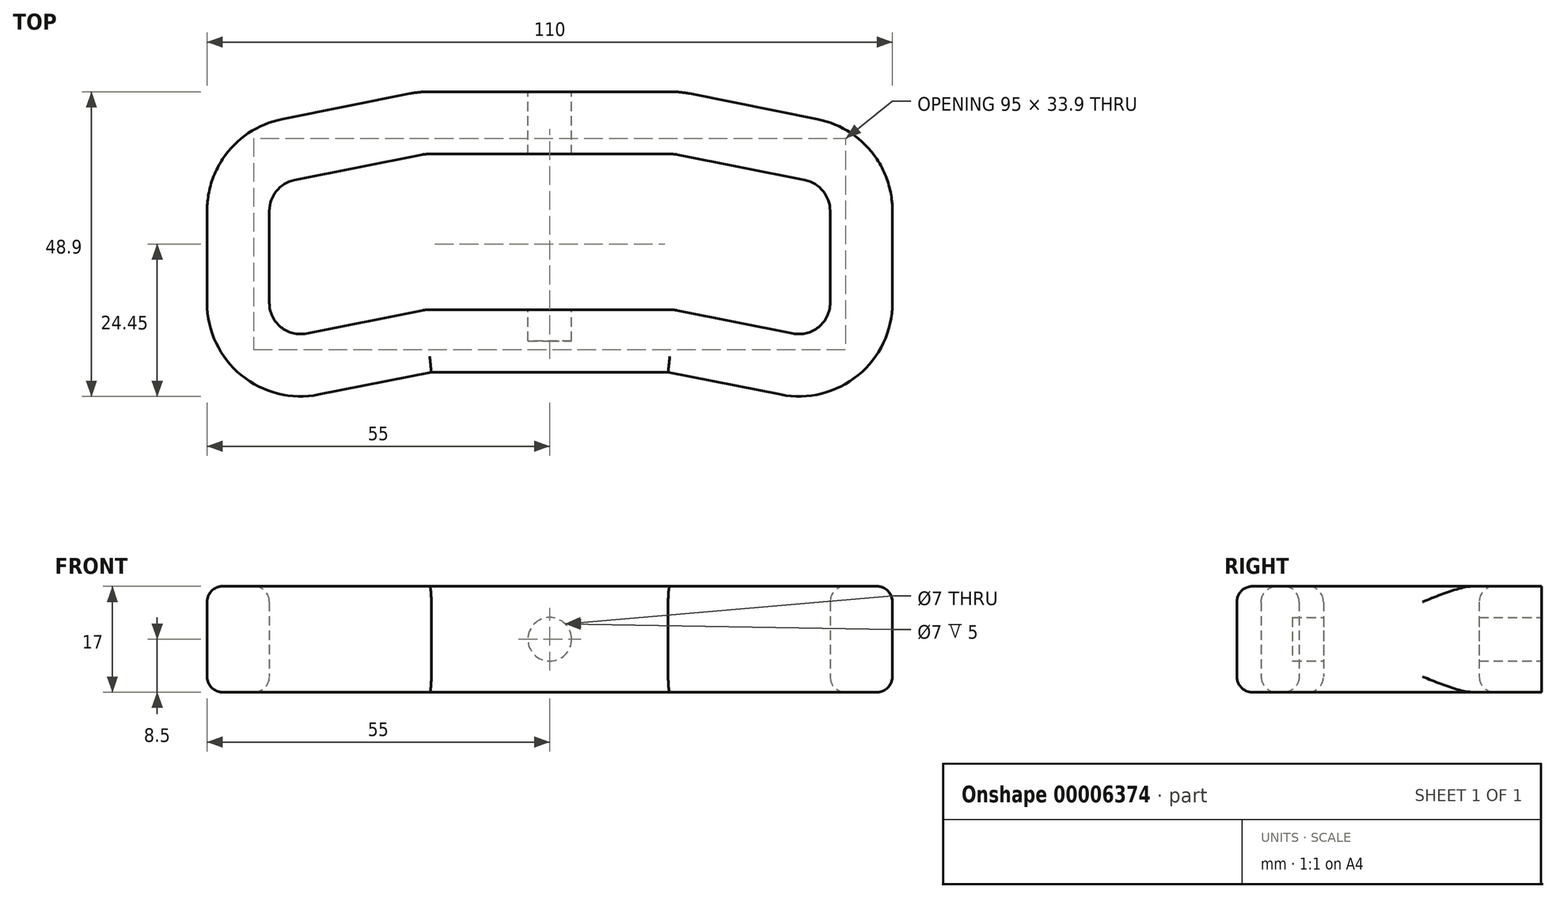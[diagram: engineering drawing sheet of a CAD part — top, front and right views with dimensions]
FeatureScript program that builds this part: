
annotation { "Feature Type Name" : "Feature", "Feature Type Description" : "" }
export const myFeature = defineFeature(function(context is Context, id is Id, definition is map)
    precondition{}
    {
        {
            var Q0;
            Q0=qCreatedBy(makeId("Top.planeOp"),FACE);
            var sketch = newSketch(context, id + "F0", { "sketchPlane" : qUnion([Q0])});
            skLineSegment(sketch, "E0.bottom", {"start": v(-45, 30) * mm, "end": v(45, 30) * mm, "construction": true});
            skLineSegment(sketch, "E0.top", {"start": v(-45, 0) * mm, "end": v(45, 0) * mm, "construction": true});
            skLineSegment(sketch, "E0.left", {"start": v(-45, 30) * mm, "end": v(-45, 0) * mm, "construction": true});
            skLineSegment(sketch, "E0.right", {"start": v(45, 30) * mm, "end": v(45, 0) * mm, "construction": true});
            skLineSegment(sketch, "E1.bottom", {"start": v(-20, 30) * mm, "end": v(20, 30) * mm, "construction": true});
            skLineSegment(sketch, "E1.top", {"start": v(-20, 0) * mm, "end": v(20, 0) * mm, "construction": true});
            skLineSegment(sketch, "E1.left", {"start": v(-20, 30) * mm, "end": v(-20, 0) * mm, "construction": true});
            skLineSegment(sketch, "E1.right", {"start": v(20, 30) * mm, "end": v(20, 0) * mm, "construction": true});
            skLineSegment(sketch, "E2.bottom", {"start": v(-45, 25) * mm, "end": v(45, 25) * mm, "construction": true});
            skLineSegment(sketch, "E2.top", {"start": v(-45, 5) * mm, "end": v(45, 5) * mm, "construction": true});
            skLineSegment(sketch, "E2.left", {"start": v(-45, 25) * mm, "end": v(-45, 5) * mm, "construction": true});
            skLineSegment(sketch, "E2.right", {"start": v(45, 25) * mm, "end": v(45, 5) * mm, "construction": true});
            skLineSegment(sketch, "E3", {"start": v(-40.98, 25.8) * mm, "end": v(-20.49, 29.9) * mm});
            skLineSegment(sketch, "E4", {"start": v(20.49, 29.9) * mm, "end": v(40.98, 25.8) * mm});
            skLineSegment(sketch, "E5", {"start": v(-19.5, 30) * mm, "end": v(19.5, 30) * mm});
            skLineSegment(sketch, "E6", {"start": v(39.02, 1.2) * mm, "end": v(20.49, 4.9) * mm});
            skLineSegment(sketch, "E7", {"start": v(-19.5, 5) * mm, "end": v(19.5, 5) * mm});
            skLineSegment(sketch, "E8", {"start": v(-20.49, 4.9) * mm, "end": v(-39.02, 1.2) * mm});
            skLineSegment(sketch, "E9", {"start": v(-45, 6.1) * mm, "end": v(-45, 20.9) * mm});
            skPoint(sketch, "E10.visualSharp", {"position": v(-45, 25) * mm});
            skArc(sketch, "E10.filletArc", {"start": v(-40.98, 25.8) * mm, "mid": v(-43.87, 24.07) * mm, "end": v(-45, 20.9) * mm});
            skPoint(sketch, "E11.visualSharp", {"position": v(-45, 0) * mm});
            skArc(sketch, "E11.filletArc", {"start": v(-45, 6.1) * mm, "mid": v(-43.17, 2.23) * mm, "end": v(-39.02, 1.2) * mm});
            skPoint(sketch, "E12.visualSharp", {"position": v(-20, 5) * mm});
            skArc(sketch, "E12.filletArc", {"start": v(-19.5, 5) * mm, "mid": v(-20, 4.98) * mm, "end": v(-20.49, 4.9) * mm});
            skPoint(sketch, "E13.visualSharp", {"position": v(20, 5) * mm});
            skArc(sketch, "E13.filletArc", {"start": v(20.49, 4.9) * mm, "mid": v(20, 4.98) * mm, "end": v(19.5, 5) * mm});
            skLineSegment(sketch, "E14", {"start": v(45, 6.1) * mm, "end": v(45, 20.9) * mm});
            skPoint(sketch, "E15.visualSharp", {"position": v(45, 0) * mm});
            skArc(sketch, "E15.filletArc", {"start": v(39.02, 1.2) * mm, "mid": v(43.17, 2.23) * mm, "end": v(45, 6.1) * mm});
            skPoint(sketch, "E16.visualSharp", {"position": v(45, 25) * mm});
            skArc(sketch, "E16.filletArc", {"start": v(45, 20.9) * mm, "mid": v(43.87, 24.07) * mm, "end": v(40.98, 25.8) * mm});
            skPoint(sketch, "E17.visualSharp", {"position": v(20, 30) * mm});
            skArc(sketch, "E17.filletArc", {"start": v(20.49, 29.9) * mm, "mid": v(20, 29.98) * mm, "end": v(19.5, 30) * mm});
            skPoint(sketch, "E18.visualSharp", {"position": v(-20, 30) * mm});
            skArc(sketch, "E18.filletArc", {"start": v(-19.5, 30) * mm, "mid": v(-20, 29.98) * mm, "end": v(-20.49, 29.9) * mm});
            skArc(sketch, "E19.0", {"start": v(-55, 6.1) * mm, "mid": v(-49.5, -5.5) * mm, "end": v(-37.06, -8.6) * mm});
            skLineSegment(sketch, "E19.1", {"start": v(-19, -5) * mm, "end": v(-37.06, -8.6) * mm});
            skLineSegment(sketch, "E19.2", {"start": v(-19, -5) * mm, "end": v(19, -5) * mm});
            skLineSegment(sketch, "E19.3", {"start": v(37.06, -8.6) * mm, "end": v(19, -5) * mm});
            skArc(sketch, "E19.4", {"start": v(37.06, -8.6) * mm, "mid": v(49.5, -5.5) * mm, "end": v(55, 6.1) * mm});
            skLineSegment(sketch, "E19.5", {"start": v(-55, 6.1) * mm, "end": v(-55, 20.9) * mm});
            skLineSegment(sketch, "E19.6", {"start": v(55, 6.1) * mm, "end": v(55, 20.9) * mm});
            skArc(sketch, "E19.7", {"start": v(55, 20.9) * mm, "mid": v(51.6, 30.41) * mm, "end": v(42.94, 35.6) * mm});
            skLineSegment(sketch, "E19.8", {"start": v(22.45, 39.7) * mm, "end": v(42.94, 35.6) * mm});
            skArc(sketch, "E19.9", {"start": v(22.45, 39.7) * mm, "mid": v(20.98, 39.93) * mm, "end": v(19.5, 40) * mm});
            skLineSegment(sketch, "E19.10", {"start": v(-19.5, 40) * mm, "end": v(19.5, 40) * mm});
            skArc(sketch, "E19.11", {"start": v(-19.5, 40) * mm, "mid": v(-20.98, 39.93) * mm, "end": v(-22.45, 39.7) * mm});
            skLineSegment(sketch, "E19.12", {"start": v(-42.94, 35.6) * mm, "end": v(-22.45, 39.7) * mm});
            skArc(sketch, "E19.13", {"start": v(-42.94, 35.6) * mm, "mid": v(-51.6, 30.41) * mm, "end": v(-55, 20.9) * mm});
            skLineSegment(sketch, "E20", {"start": v(-221.78, -63.4) * mm, "end": v(-201.28, -59.3) * mm});
            skLineSegment(sketch, "E21", {"start": v(-200.3, -59.2) * mm, "end": v(-161.3, -59.2) * mm});
            skLineSegment(sketch, "E22", {"start": v(-200.3, -84.2) * mm, "end": v(-161.3, -84.2) * mm});
            skLineSegment(sketch, "E23", {"start": v(-201.28, -84.3) * mm, "end": v(-219.82, -88) * mm});
            skLineSegment(sketch, "E24", {"start": v(-225.8, -83.1) * mm, "end": v(-225.8, -68.3) * mm});
            skPoint(sketch, "E25.visualSharp", {"position": v(-225.8, -64.2) * mm});
            skArc(sketch, "E25.filletArc", {"start": v(-221.78, -63.4) * mm, "mid": v(-224.66, -65.13) * mm, "end": v(-225.8, -68.3) * mm});
            skPoint(sketch, "E26.visualSharp", {"position": v(-225.8, -89.2) * mm});
            skArc(sketch, "E26.filletArc", {"start": v(-225.8, -83.1) * mm, "mid": v(-223.97, -86.97) * mm, "end": v(-219.82, -88) * mm});
            skPoint(sketch, "E27.visualSharp", {"position": v(-200.8, -84.2) * mm});
            skArc(sketch, "E27.filletArc", {"start": v(-200.3, -84.2) * mm, "mid": v(-200.8, -84.22) * mm, "end": v(-201.28, -84.3) * mm});
            skPoint(sketch, "E28.visualSharp", {"position": v(-200.8, -59.2) * mm});
            skArc(sketch, "E28.filletArc", {"start": v(-200.3, -59.2) * mm, "mid": v(-200.8, -59.22) * mm, "end": v(-201.28, -59.3) * mm});
            skArc(sketch, "E29.0", {"start": v(-235.8, -83.1) * mm, "mid": v(-234.65, -88.85) * mm, "end": v(-231.38, -93.73) * mm});
            skLineSegment(sketch, "E29.5", {"start": v(-235.8, -83.1) * mm, "end": v(-235.8, -68.3) * mm});
            skLineSegment(sketch, "E29.10", {"start": v(-200.3, -49.2) * mm, "end": v(-161.3, -49.2) * mm, "construction": true});
            skArc(sketch, "E29.11", {"start": v(-200.3, -49.2) * mm, "mid": v(-201.78, -49.27) * mm, "end": v(-203.24, -49.5) * mm, "construction": true});
            skLineSegment(sketch, "E29.12", {"start": v(-223.74, -53.6) * mm, "end": v(-203.24, -49.5) * mm, "construction": true});
            skArc(sketch, "E29.13", {"start": v(-223.74, -53.6) * mm, "mid": v(-232.4, -58.79) * mm, "end": v(-235.8, -68.3) * mm, "construction": true});
            skPoint(sketch, "E30", {"position": v(-231.38, -93.73) * mm});
            skLineSegment(sketch, "E31.MirrorCS", {"start": v(-200.8, -44.2) * mm, "end": v(-160.8, -44.2) * mm});
            skLineSegment(sketch, "E32.MirrorCS", {"start": v(-235.8, -65.3) * mm, "end": v(-235.8, -80.1) * mm});
            skArc(sketch, "E33.MirrorCS", {"start": v(-235.8, -65.3) * mm, "mid": v(-233.22, -56.89) * mm, "end": v(-226.37, -51.37) * mm});
            skLineSegment(sketch, "E34", {"start": v(-231.38, -93.73) * mm, "end": v(-202.8, -122.21) * mm});
            skLineSegment(sketch, "E35", {"start": v(-200.8, -44.2) * mm, "end": v(-226.37, -51.37) * mm});
            skArc(sketch, "E36", {"start": v(-200.8, -44.2) * mm, "mid": v(-194.13, -49.2) * mm, "end": v(-187.46, -44.2) * mm, "construction": true});
            skArc(sketch, "E37", {"start": v(-187.46, -44.2) * mm, "mid": v(-180.8, -49.2) * mm, "end": v(-174.13, -44.2) * mm, "construction": true});
            skArc(sketch, "E38", {"start": v(-213.64, -47.8) * mm, "mid": v(-206.08, -50.04) * mm, "end": v(-200.8, -44.2) * mm, "construction": true});
            skArc(sketch, "E39", {"start": v(-226.47, -51.4) * mm, "mid": v(-219.2, -52.66) * mm, "end": v(-213.64, -47.8) * mm, "construction": true});
            skArc(sketch, "E40", {"start": v(-235.28, -61.4) * mm, "mid": v(-230.53, -56.71) * mm, "end": v(-226.47, -51.4) * mm, "construction": true});
            skPoint(sketch, "E41.visualSharp", {"position": v(-200.8, -124.2) * mm});
            skArc(sketch, "E41.filletArc", {"start": v(-202.8, -122.21) * mm, "mid": v(-200.23, -123.83) * mm, "end": v(-197.21, -124.2) * mm});
            skLineSegment(sketch, "E42.4", {"start": v(-200.3, -62.4) * mm, "end": v(-161.3, -62.4) * mm, "construction": true});
            skArc(sketch, "E42.5", {"start": v(-200.3, -62.4) * mm, "mid": v(-200.48, -62.4) * mm, "end": v(-200.66, -62.43) * mm});
            skLineSegment(sketch, "E42.6", {"start": v(-221.15, -66.53) * mm, "end": v(-200.66, -62.43) * mm, "construction": true});
            skArc(sketch, "E42.7", {"start": v(-221.15, -66.53) * mm, "mid": v(-222.2, -67.16) * mm, "end": v(-222.6, -68.3) * mm, "construction": true});
            skLineSegment(sketch, "E42.8", {"start": v(-222.6, -83.1) * mm, "end": v(-222.6, -68.3) * mm, "construction": true});
            skArc(sketch, "E42.9", {"start": v(-222.6, -83.1) * mm, "mid": v(-221.94, -84.5) * mm, "end": v(-220.45, -84.87) * mm, "construction": true});
            skLineSegment(sketch, "E42.10", {"start": v(-201.91, -81.16) * mm, "end": v(-220.45, -84.87) * mm, "construction": true});
            skArc(sketch, "E42.11", {"start": v(-200.3, -81) * mm, "mid": v(-201.11, -81.04) * mm, "end": v(-201.91, -81.16) * mm, "construction": true});
            skLineSegment(sketch, "E42.12", {"start": v(-200.3, -81) * mm, "end": v(-161.3, -81) * mm, "construction": true});
            skLineSegment(sketch, "E43", {"start": v(-180.8, -42.26) * mm, "end": v(-180.8, -30.31) * mm, "construction": true});
            skArc(sketch, "E44.MirrorCS", {"start": v(-161.3, -84.2) * mm, "mid": v(-160.8, -84.22) * mm, "end": v(-160.31, -84.3) * mm});
            skArc(sketch, "E45.MirrorCS", {"start": v(-161.3, -59.2) * mm, "mid": v(-160.8, -59.22) * mm, "end": v(-160.31, -59.3) * mm});
            skArc(sketch, "E46.MirrorCS", {"start": v(-140.45, -66.53) * mm, "mid": v(-139.4, -67.16) * mm, "end": v(-139, -68.3) * mm, "construction": true});
            skArc(sketch, "E47.MirrorCS", {"start": v(-161.3, -49.2) * mm, "mid": v(-159.82, -49.27) * mm, "end": v(-158.35, -49.5) * mm, "construction": true});
            skArc(sketch, "E48.MirrorCS", {"start": v(-161.3, -62.4) * mm, "mid": v(-161.12, -62.4) * mm, "end": v(-160.94, -62.43) * mm});
            skArc(sketch, "E49.MirrorCS", {"start": v(-139, -83.1) * mm, "mid": v(-139.66, -84.5) * mm, "end": v(-141.15, -84.87) * mm, "construction": true});
            skArc(sketch, "E50.MirrorCS", {"start": v(-161.3, -81) * mm, "mid": v(-160.49, -81.04) * mm, "end": v(-159.68, -81.16) * mm, "construction": true});
            skLineSegment(sketch, "E51.MirrorCS", {"start": v(-125.8, -65.3) * mm, "end": v(-125.8, -80.1) * mm});
            skPoint(sketch, "E52.MirrorP", {"position": v(-135.8, -64.2) * mm});
            skArc(sketch, "E53.MirrorCS", {"start": v(-147.96, -47.8) * mm, "mid": v(-155.51, -50.04) * mm, "end": v(-160.8, -44.2) * mm, "construction": true});
            skLineSegment(sketch, "E54.MirrorCS", {"start": v(-159.68, -81.16) * mm, "end": v(-141.15, -84.87) * mm, "construction": true});
            skLineSegment(sketch, "E55.MirrorCS", {"start": v(-160.31, -84.3) * mm, "end": v(-141.78, -88) * mm});
            skLineSegment(sketch, "E56.MirrorCS", {"start": v(-130.21, -93.73) * mm, "end": v(-158.8, -122.21) * mm});
            skLineSegment(sketch, "E57.MirrorCS", {"start": v(-140.45, -66.53) * mm, "end": v(-160.94, -62.43) * mm, "construction": true});
            skPoint(sketch, "E58.MirrorP", {"position": v(-135.8, -89.2) * mm});
            skPoint(sketch, "E59.MirrorP", {"position": v(-160.8, -124.2) * mm});
            skLineSegment(sketch, "E60.MirrorCS", {"start": v(-125.8, -83.1) * mm, "end": v(-125.8, -68.3) * mm});
            skArc(sketch, "E61.MirrorCS", {"start": v(-135.12, -51.4) * mm, "mid": v(-142.4, -52.66) * mm, "end": v(-147.96, -47.8) * mm, "construction": true});
            skArc(sketch, "E62.MirrorCS", {"start": v(-160.8, -44.2) * mm, "mid": v(-167.46, -49.2) * mm, "end": v(-174.13, -44.2) * mm, "construction": true});
            skArc(sketch, "E63.MirrorCS", {"start": v(-126.31, -61.4) * mm, "mid": v(-131.07, -56.71) * mm, "end": v(-135.12, -51.4) * mm, "construction": true});
            skArc(sketch, "E64.MirrorCS", {"start": v(-158.8, -122.21) * mm, "mid": v(-161.37, -123.83) * mm, "end": v(-164.38, -124.2) * mm});
            skLineSegment(sketch, "E65.MirrorCS", {"start": v(-160.8, -44.2) * mm, "end": v(-135.23, -51.37) * mm});
            skPoint(sketch, "E66.MirrorP", {"position": v(-130.21, -93.73) * mm});
            skArc(sketch, "E67.MirrorCS", {"start": v(-125.8, -65.3) * mm, "mid": v(-128.38, -56.89) * mm, "end": v(-135.23, -51.37) * mm});
            skLineSegment(sketch, "E68.MirrorCS", {"start": v(-135.8, -83.1) * mm, "end": v(-135.8, -68.3) * mm});
            skArc(sketch, "E69.MirrorCS", {"start": v(-125.8, -83.1) * mm, "mid": v(-126.95, -88.85) * mm, "end": v(-130.21, -93.73) * mm});
            skPoint(sketch, "E70.MirrorP", {"position": v(-160.8, -84.2) * mm});
            skLineSegment(sketch, "E71.MirrorCS", {"start": v(-139.82, -63.4) * mm, "end": v(-160.31, -59.3) * mm});
            skLineSegment(sketch, "E72.MirrorCS", {"start": v(-137.86, -53.6) * mm, "end": v(-158.35, -49.5) * mm, "construction": true});
            skArc(sketch, "E73.MirrorCS", {"start": v(-135.8, -83.1) * mm, "mid": v(-137.63, -86.97) * mm, "end": v(-141.78, -88) * mm});
            skPoint(sketch, "E74.MirrorP", {"position": v(-160.8, -59.2) * mm});
            skArc(sketch, "E75.MirrorCS", {"start": v(-139.82, -63.4) * mm, "mid": v(-136.93, -65.13) * mm, "end": v(-135.8, -68.3) * mm});
            skLineSegment(sketch, "E76.MirrorCS", {"start": v(-139, -83.1) * mm, "end": v(-139, -68.3) * mm, "construction": true});
            skArc(sketch, "E77.MirrorCS", {"start": v(-137.86, -53.6) * mm, "mid": v(-129.2, -58.79) * mm, "end": v(-125.8, -68.3) * mm, "construction": true});
            skLineSegment(sketch, "E78", {"start": v(-197.21, -124.2) * mm, "end": v(-164.38, -124.2) * mm});
            skSolve(sketch);
        }
        {
            var Q0;
            Q0=makeQuery(id+"F0.imprint","IMPRINT",FACE,{"disambiguationData":[TD([[makeQuery(id+"F0.imprint","IMPRINT",EDGE,{"derivedFrom":sQuery(id+"F0.wireOp",EDGE,"E3")}),1.0]])]});
            extrude(context, id + "F1", {"entities" : qUnion([Q0]), "depth" : 17 * mm});
        }
        {
            var Q0;
            Q0=makeQuery(id+"F1.opExtrude","SWEPT_FACE",FACE,{"disambiguationData":[OSD([sQuery(id+"F0.wireOp",EDGE,"E19.10")])]});
            var sketch = newSketch(context, id + "F2", { "sketchPlane" : qUnion([Q0])});
            skLineSegment(sketch, "E79", {"start": v(-19.5, 17) * mm, "end": v(19.5, 0) * mm, "construction": true});
            skLineSegment(sketch, "E80", {"start": v(19.5, 17) * mm, "end": v(-19.5, 0) * mm, "construction": true});
            skCircle(sketch, "E81", {"center": v(0, 8.5) * mm, "radius": 3.5 * mm});
            skSolve(sketch);
        }
        {
            var Q0;
            Q0=makeQuery(id+"F2.imprint","IMPRINT",FACE,{"disambiguationData":[TD([[makeQuery(id+"F2.imprint","IMPRINT",EDGE,{"derivedFrom":sQuery(id+"F2.wireOp",EDGE,"E81")}),1.0]])]});
            extrude(context, id + "F3", {"entities" : qUnion([Q0]), "operationType" : NewBodyOperationType.REMOVE, "oppositeDirection" : true, "depth" : 40 * mm});
        }
        {
            var Q0;
            Q0=makeQuery(id+"F1.opExtrude","CAP_EDGE",EDGE,{"disambiguationData":[OSD([sQuery(id+"F0.wireOp",EDGE,"E5")])],"isStart":true});
            var Q1;
            Q1=makeQuery(id+"F1.opExtrude","CAP_EDGE",EDGE,{"disambiguationData":[OSD([sQuery(id+"F0.wireOp",EDGE,"E5")])],"isStart":false});
            fillet(context, id + "F4", {"entities" : qUnion([Q0, Q1]), "radius" : 2.5 * mm, "tangentPropagation" : true, "allowEdgeOverflow" : false});
        }
        {
            var Q0;
            Q0=makeQuery(id+"F1.opExtrude","CAP_EDGE",EDGE,{"disambiguationData":[OSD([sQuery(id+"F0.wireOp",EDGE,"E19.5")])],"isStart":false});
            var Q1;
            Q1=makeQuery(id+"F1.opExtrude","CAP_EDGE",EDGE,{"disambiguationData":[OSD([sQuery(id+"F0.wireOp",EDGE,"E19.0")])],"isStart":false});
            var Q2;
            Q2=makeQuery(id+"F1.opExtrude","CAP_EDGE",EDGE,{"disambiguationData":[OSD([sQuery(id+"F0.wireOp",EDGE,"E19.1")])],"isStart":false});
            var Q3;
            Q3=makeQuery(id+"F1.opExtrude","CAP_EDGE",EDGE,{"disambiguationData":[OSD([sQuery(id+"F0.wireOp",EDGE,"E19.2")])],"isStart":false});
            var Q4;
            Q4=makeQuery(id+"F1.opExtrude","CAP_EDGE",EDGE,{"disambiguationData":[OSD([sQuery(id+"F0.wireOp",EDGE,"E19.3")])],"isStart":false});
            var Q5;
            Q5=makeQuery(id+"F1.opExtrude","CAP_EDGE",EDGE,{"disambiguationData":[OSD([sQuery(id+"F0.wireOp",EDGE,"E19.4")])],"isStart":false});
            var Q6;
            Q6=makeQuery(id+"F1.opExtrude","CAP_EDGE",EDGE,{"disambiguationData":[OSD([sQuery(id+"F0.wireOp",EDGE,"E19.6")])],"isStart":false});
            var Q7;
            Q7=makeQuery(id+"F1.opExtrude","CAP_EDGE",EDGE,{"disambiguationData":[OSD([sQuery(id+"F0.wireOp",EDGE,"E19.6")])],"isStart":true});
            var Q8;
            Q8=makeQuery(id+"F1.opExtrude","CAP_EDGE",EDGE,{"disambiguationData":[OSD([sQuery(id+"F0.wireOp",EDGE,"E19.4")])],"isStart":true});
            var Q9;
            Q9=makeQuery(id+"F1.opExtrude","CAP_EDGE",EDGE,{"disambiguationData":[OSD([sQuery(id+"F0.wireOp",EDGE,"E19.3")])],"isStart":true});
            var Q10;
            Q10=makeQuery(id+"F1.opExtrude","CAP_EDGE",EDGE,{"disambiguationData":[OSD([sQuery(id+"F0.wireOp",EDGE,"E19.2")])],"isStart":true});
            var Q11;
            Q11=makeQuery(id+"F1.opExtrude","CAP_EDGE",EDGE,{"disambiguationData":[OSD([sQuery(id+"F0.wireOp",EDGE,"E19.1")])],"isStart":true});
            var Q12;
            Q12=makeQuery(id+"F1.opExtrude","CAP_EDGE",EDGE,{"disambiguationData":[OSD([sQuery(id+"F0.wireOp",EDGE,"E19.0")])],"isStart":true});
            var Q13;
            Q13=makeQuery(id+"F1.opExtrude","CAP_EDGE",EDGE,{"disambiguationData":[OSD([sQuery(id+"F0.wireOp",EDGE,"E19.5")])],"isStart":true});
            fillet(context, id + "F5", {"entities" : qUnion([Q0, Q1, Q2, Q3, Q4, Q5, Q6, Q7, Q8, Q9, Q10, Q11, Q12, Q13]), "radius" : 2.5 * mm, "allowEdgeOverflow" : false});
        }
    });
